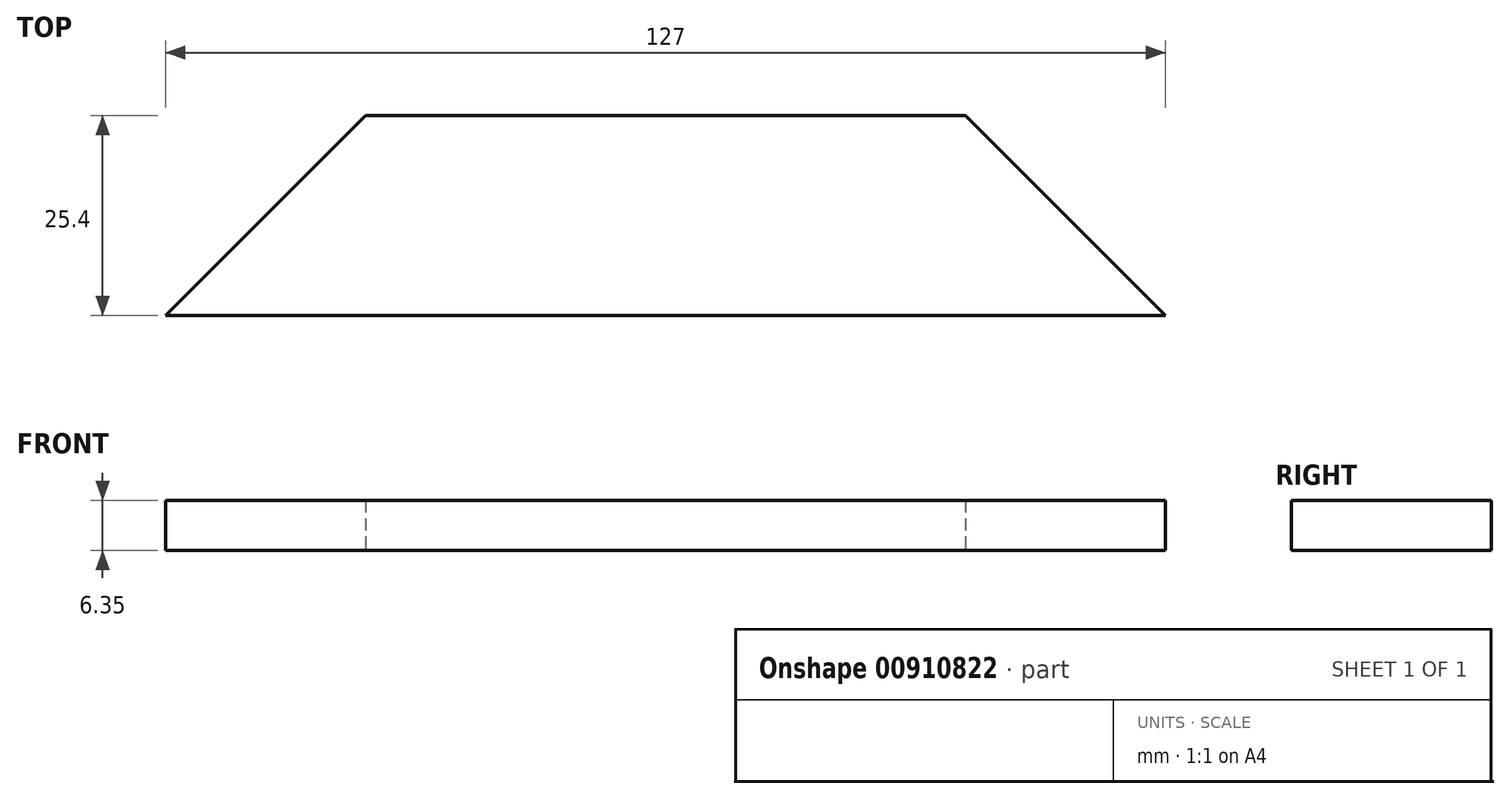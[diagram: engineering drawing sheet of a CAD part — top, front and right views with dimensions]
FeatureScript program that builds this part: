
annotation { "Feature Type Name" : "Feature", "Feature Type Description" : "" }
export const myFeature = defineFeature(function(context is Context, id is Id, definition is map)
    precondition{}
    {
        {
            var Q0;
            Q0=qCreatedBy(makeId("Top.planeOp"),FACE);
            var sketch = newSketch(context, id + "F0", { "sketchPlane" : qUnion([Q0])});
            skLineSegment(sketch, "E0.bottom", {"start": v(0, 0) * mm, "end": v(127, 0) * mm});
            skLineSegment(sketch, "E0.top", {"start": v(25.4, 25.4) * mm, "end": v(101.6, 25.4) * mm});
            skLineSegment(sketch, "E1", {"start": v(0, 0) * mm, "end": v(25.4, 25.4) * mm});
            skLineSegment(sketch, "E2", {"start": v(127, 0) * mm, "end": v(101.6, 25.4) * mm});
            skSolve(sketch);
        }
        {
            var Q0;
            Q0 = qSketchRegion(id + "F0", true);
            extrude(context, id + "F1", {"entities" : qUnion([Q0]), "depth" : 6.35 * mm, "offsetDistance" : 25.4 * mm});
        }
    });
